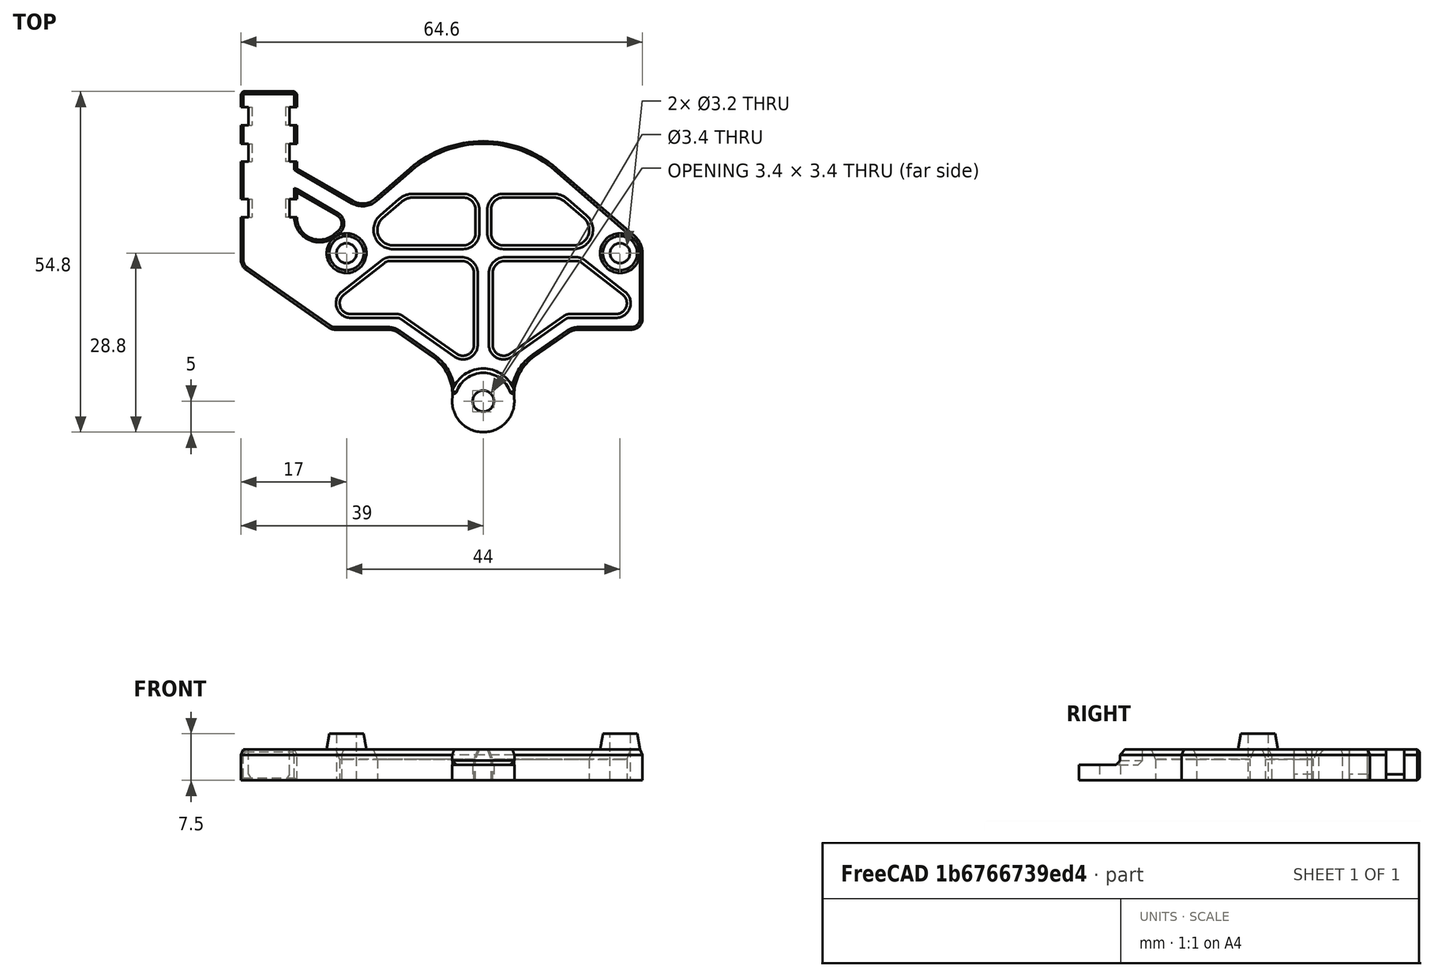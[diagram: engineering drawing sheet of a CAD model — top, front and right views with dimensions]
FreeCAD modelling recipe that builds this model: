
FCSTD DOCUMENT  (FreeCAD 0.21R33771 (Git))
Label: StrainRelief_v4
License: All rights reserved
LicenseURL: https://en.wikipedia.org/wiki/All_rights_reserved
objects: Sketcher::SketchObject×6, Part::Chamfer×5, PartDesign::Pad×3, PartDesign::Pocket×2, PartDesign::Body×2, Part::Fillet×2, Mesh::Feature×1, PartDesign::Mirrored×1, PartDesign::Chamfer×1, Part::Fuse×1
note: 29 computed .brp shape members not serialized (recipe doc carries the construction recipe); baked Part::Feature solids carry a one-line shape summary decoded from their .brp

FEATURE [Mesh::Feature] EBB36_Mount___Sherpa_Mini  label="EBB36 Mount - Sherpa-Mini"
  Placement = pos=(-216.5,184.28,0) rot=(0,0,1;4.71239rad)
FEATURE [Sketcher::SketchObject] Sketch
  FullyConstrained = true
  MapMode = 5
  Support = -> [XY_Plane]
  sketch-geometry (31):
    g0: ArcOfCircle CenterX=0 CenterY=-23.8 CenterZ=0 NormalX=0 NormalY=0 NormalZ=1 AngleXU=0 Radius=1.7 StartAngle=1.5708 EndAngle=4.71239
    g1: LineSegment StartX=-15.35 StartY=-12.3 StartZ=0 EndX=-23.85 EndY=-12.3 EndZ=0
    g2: ArcOfCircle CenterX=-23.85 CenterY=-10.55 CenterZ=0 NormalX=0 NormalY=0 NormalZ=1 AngleXU=0 Radius=1.75 StartAngle=3.14159 EndAngle=4.71239
    g3: LineSegment StartX=-25.6 StartY=-10.55 StartZ=0 EndX=-25.6 EndY=0 EndZ=0
    g4: ArcOfCircle CenterX=-22 CenterY=0 CenterZ=0 NormalX=0 NormalY=0 NormalZ=1 AngleXU=0 Radius=3.6 StartAngle=2.28438 EndAngle=3.14159
    g5: ArcOfCircle CenterX=0 CenterY=0 CenterZ=0 NormalX=0 NormalY=0 NormalZ=1 AngleXU=0 Radius=18 StartAngle=1.5708 EndAngle=2.28438
    g6: LineSegment StartX=0 StartY=18 StartZ=0 EndX=0 EndY=-22.1 EndZ=0
    g7: LineSegment StartX=-3e-16 StartY=-25.5 StartZ=0 EndX=0 EndY=-28.8 EndZ=0
    g8: ArcOfCircle CenterX=0 CenterY=-23.8 CenterZ=0 NormalX=0 NormalY=0 NormalZ=1 AngleXU=0 Radius=5 StartAngle=3.06281 EndAngle=4.71239
    g9: ArcOfCircle CenterX=-12.4612 CenterY=-22.8162 CenterZ=0 NormalX=0 NormalY=0 NormalZ=1 AngleXU=0 Radius=7.5 StartAngle=6.2044 EndAngle=7.24312
    g10: LineSegment StartX=-8.1594 StartY=-16.6726 StartZ=0 EndX=-13.6293 EndY=-12.8425 EndZ=0
    g11: LineSegment StartX=-12.9829 StartY=-10.0713 StartZ=0 EndX=-4.25376 EndY=-16.1835 EndZ=0
    g12: LineSegment StartX=-13.8433 StartY=-9.8 StartZ=0 EndX=-21.35 EndY=-9.8 EndZ=0
    g13: ArcOfCircle CenterX=-21.35 CenterY=-8.05 CenterZ=0 NormalX=0 NormalY=0 NormalZ=1 AngleXU=0 Radius=1.75 StartAngle=2.23402 EndAngle=4.71239
    g14: LineSegment StartX=-22.4274 StartY=-6.67098 StartZ=0 EndX=-15.8959 EndY=-1.56798 EndZ=0
    g15: LineSegment StartX=-14.9724 StartY=-1.25 StartZ=0 EndX=-3.5 EndY=-1.25 EndZ=0
    g16: ArcOfCircle CenterX=-3.5 CenterY=-3.25 CenterZ=0 NormalX=0 NormalY=0 NormalZ=1 AngleXU=0 Radius=2 StartAngle=1e-16 EndAngle=1.5708
    g17: LineSegment StartX=-1.5 StartY=-3.25 StartZ=0 EndX=-1.5 EndY=-14.75 EndZ=0
    g18: ArcOfCircle CenterX=-3.25 CenterY=-14.75 CenterZ=0 NormalX=0 NormalY=0 NormalZ=1 AngleXU=0 Radius=1.75 StartAngle=4.10152 EndAngle=6.28319
    g19: LineSegment StartX=-1.25 StartY=6.95 StartZ=0 EndX=-1.25 EndY=3.25 EndZ=0
    g20: ArcOfCircle CenterX=-3.25 CenterY=3.25 CenterZ=0 NormalX=0 NormalY=0 NormalZ=1 AngleXU=0 Radius=2 StartAngle=4.71239 EndAngle=6.28319
    g21: LineSegment StartX=-3.25 StartY=1.25 StartZ=0 EndX=-14.5429 EndY=1.25 EndZ=0
    g22: ArcOfCircle CenterX=-3.25 CenterY=6.95 CenterZ=0 NormalX=0 NormalY=0 NormalZ=1 AngleXU=0 Radius=2 StartAngle=2e-16 EndAngle=1.5708
    g23: LineSegment StartX=-3.25 StartY=8.95 StartZ=0 EndX=-11.25 EndY=8.95 EndZ=0
    g24: ArcOfCircle CenterX=-14.5429 CenterY=3.75 CenterZ=0 NormalX=0 NormalY=0 NormalZ=1 AngleXU=0 Radius=2.5 StartAngle=2.28638 EndAngle=4.71239
    g25: ArcOfCircle CenterX=-11.25 CenterY=5.95 CenterZ=0 NormalX=0 NormalY=0 NormalZ=1 AngleXU=0 Radius=3 StartAngle=1.5708 EndAngle=2.28638
    g26: LineSegment StartX=-16.1831 StartY=5.63677 StartZ=0 EndX=-13.2182 EndY=8.21413 EndZ=0
    g27: ArcOfCircle CenterX=-13.8433 CenterY=-11.3 CenterZ=0 NormalX=0 NormalY=0 NormalZ=1 AngleXU=0 Radius=1.5 StartAngle=0.959931 EndAngle=1.5708
    g28: ArcOfCircle CenterX=-15.35 CenterY=-15.3 CenterZ=0 NormalX=0 NormalY=0 NormalZ=1 AngleXU=0 Radius=3 StartAngle=0.959931 EndAngle=1.5708
    g29: ArcOfCircle CenterX=-14.9724 CenterY=-2.75 CenterZ=0 NormalX=0 NormalY=0 NormalZ=1 AngleXU=0 Radius=1.5 StartAngle=1.5708 EndAngle=2.23402
    g30: LineSegment StartX=-24.3564 StartY=2.72168 StartZ=0 EndX=-11.7818 EndY=13.6084 EndZ=0
  constraints (79):
    c: PointOnObject(g0,g-2)
    c: Diameter(g0) = 3.4
    c: Horizontal(g1)
    c: Tangent(g1,g2) = 1.5708
    c: PointOnObject(g3,g-1)
    c: Tangent(g3,g4) = 1.5708
    c: PointOnObject(g5,g-2)
    c: DistanceY(g5,g5) = 18
    c: DistanceY(g1,g5) = 12.3
    c: Tangent(g2,g3) = 1.5708
    c: Coincident(g6,g5)
    c: Vertical(g6)
    c: Perpendicular(g7,g8) = 1.5708
    c: Coincident(g8,g0)
    c: PointOnObject(g7,g-2)
    c: Coincident(g0,g7)
    c: Coincident(g0,g6)
    c: Coincident(g5,g-1)
    c: DistanceY(g0,g5) = 23.8
    c: Diameter(g8) = 10
    c: Tangent(g8,g9) = 1.5708
    c: Tangent(g9,g10) = -1.5708
    c: Angle(g6,g10) = 0.959931
    c: Diameter(g9) = 15
    c: Diameter(g2) = 3.5
    c: Parallel(g11,g10)
    c: Horizontal(g12)
    c: Tangent(g12,g13) = 1.5708
    c: Horizontal(g15)
    c: Tangent(g15,g16) = 1.5708
    c: Vertical(g17)
    c: Diameter(g16) = 4
    c: Tangent(g13,g14) = 1.5708
    c: Tangent(g16,g17) = 1.5708
    c: DistanceY(g15,g5) = 1.25
    c: DistanceX(g16,g5) = 1.5
    c: Tangent(g18,g17) = 1.5708
    c: Tangent(g18,g11) = -1.5708
    c: Diameter(g13) = 3.5
    c: DistanceX(g2,g13) = 4.25
    c: Diameter(g18) = 3.5
    c: Vertical(g19)
    c: Tangent(g19,g20) = 1.5708
    c: Tangent(g20,g21) = 1.5708
    c: Horizontal(g21)
    c: DistanceY(g5,g20) = 1.25
    c: DistanceX(g19,g5) = 1.25
    c: Diameter(g20) = 4
    c: Diameter(g22) = 4
    c: Horizontal(g23)
    c: Tangent(g23,g22) = -1.5708
    c: Tangent(g22,g19) = 1.5708
    c: Tangent(g24,g21) = 1.5708
    c: Tangent(g26,g24) = 1.5708
    c: Tangent(g26,g25) = 1.5708
    c: DistanceX(g23,g23) = 8
    c: Radius(g25) = 3
    c: Tangent(g25,g23) = -1.5708
    c: DistanceY(g19,g19) = 3.7
    c: Radius(g24) = 2.5
    c: Angle(g-1,g26) = 0.715585
    c: Tangent(g12,g27) = -1.5708
    c: Tangent(g11,g27) = 1.5708
    c: Tangent(g1,g28) = -1.5708
    c: Tangent(g10,g28) = -1.5708
    c: Tangent(g14,g29) = 1.5708
    c: Tangent(g15,g29) = 1.5708
    c: Radius(g29) = 1.5
    c: Radius(g27) = 1.5
    c: Radius(g28) = 3
    c: DistanceY(g1,g12) = 2.5
    c: DistanceY(g17,g17) = 11.5
    c: DistanceX(g1,g1) = 8.5
    c: Angle(g14,g6) = 0.907571
    c: DistanceX(g3,g5) = 25.6
    c: PointOnObject(g4,g-1)
    c: Diameter(g4) = 7.2
    c: Tangent(g30,g5) = 1.5708
    c: Tangent(g30,g4) = 1.5708
FEATURE [PartDesign::Pad] Pad
  Direction = (0,0,1)
  Length = 5
  Length2 = 10
  Profile = -> Sketch
  ReferenceAxis = -> Sketch [N_Axis]
  Type = 0
FEATURE [Sketcher::SketchObject] Sketch001
  AttachmentOffset = pos=(0,0,7.5) rot=(0,0,1;0rad)
  FullyConstrained = false
  MapMode = 5
  Placement = pos=(0,0,7.5) rot=(0,0,1;0rad)
  Support = -> [XY_Plane]
  sketch-geometry (1):
    g0: Circle CenterX=-22 CenterY=0 CenterZ=0 NormalX=0 NormalY=0 NormalZ=1 AngleXU=0 Radius=2.75
  constraints (2):
    c: Diameter(g0) = 5.5
    c: DistanceX(g0,g-1) = 22
FEATURE [PartDesign::Pad] Pad001
  BaseFeature = -> Pad
  Direction = (0,0,1)
  Length = 2.5
  Length2 = 10
  Profile = -> Sketch001
  ReferenceAxis = -> Sketch001 [N_Axis]
  Reversed = true
  TaperAngle = 10
  Type = 0
FEATURE [Sketcher::SketchObject] Sketch002
  FullyConstrained = true
  MapMode = 5
  Support = -> [XY_Plane]
  sketch-geometry (1):
    g0: Circle CenterX=-22 CenterY=0 CenterZ=0 NormalX=0 NormalY=0 NormalZ=1 AngleXU=0 Radius=1.6
  constraints (3):
    c: PointOnObject(g0,g-1)
    c: DistanceX(g0,g-1) = 22
    c: Diameter(g0) = 3.2
FEATURE [PartDesign::Pocket] Pocket
  BaseFeature = -> Pad001
  Direction = (0,0,-1)
  Length = 5
  Length2 = 5
  Profile = -> Sketch002
  ReferenceAxis = -> Sketch002 [N_Axis]
  Reversed = true
  Type = 1
FEATURE [PartDesign::Mirrored] Mirrored
  BaseFeature = -> Pocket
  MirrorPlane = -> Sketch [V_Axis]
  Originals = -> [Pad,Pad001,Pocket]
FEATURE [Sketcher::SketchObject] Sketch004
  FullyConstrained = true
  MapMode = 5
  Support = -> [XY_Plane001]
  sketch-geometry (31):
    g0: ArcOfCircle CenterX=0 CenterY=-23.8 CenterZ=0 NormalX=0 NormalY=0 NormalZ=1 AngleXU=0 Radius=1.7 StartAngle=1.5708 EndAngle=4.71239
    g1: LineSegment StartX=-15.35 StartY=-12.3 StartZ=0 EndX=-23.85 EndY=-12.3 EndZ=0
    g2: ArcOfCircle CenterX=-23.85 CenterY=-10.55 CenterZ=0 NormalX=0 NormalY=0 NormalZ=1 AngleXU=0 Radius=1.75 StartAngle=3.14159 EndAngle=4.71239
    g3: LineSegment StartX=-25.6 StartY=-10.55 StartZ=0 EndX=-25.6 EndY=0 EndZ=0
    g4: ArcOfCircle CenterX=-22 CenterY=0 CenterZ=0 NormalX=0 NormalY=0 NormalZ=1 AngleXU=0 Radius=3.6 StartAngle=2.28438 EndAngle=3.14159
    g5: ArcOfCircle CenterX=0 CenterY=0 CenterZ=0 NormalX=0 NormalY=0 NormalZ=1 AngleXU=0 Radius=18 StartAngle=1.5708 EndAngle=2.28438
    g6: LineSegment StartX=1e-16 StartY=18 StartZ=0 EndX=1e-16 EndY=-22.1 EndZ=0
    g7: LineSegment StartX=-2e-16 StartY=-25.5 StartZ=0 EndX=-9e-16 EndY=-28.8 EndZ=0
    g8: ArcOfCircle CenterX=0 CenterY=-23.8 CenterZ=0 NormalX=0 NormalY=0 NormalZ=1 AngleXU=0 Radius=5 StartAngle=3.06281 EndAngle=4.71239
    g9: ArcOfCircle CenterX=-12.4612 CenterY=-22.8162 CenterZ=0 NormalX=0 NormalY=0 NormalZ=1 AngleXU=0 Radius=7.5 StartAngle=6.2044 EndAngle=7.24312
    g10: LineSegment StartX=-8.1594 StartY=-16.6726 StartZ=0 EndX=-13.6293 EndY=-12.8425 EndZ=0
    g11: LineSegment StartX=-12.9829 StartY=-10.0713 StartZ=0 EndX=-4.25376 EndY=-16.1835 EndZ=0
    g12: LineSegment StartX=-13.8433 StartY=-9.8 StartZ=0 EndX=-21.35 EndY=-9.8 EndZ=0
    g13: ArcOfCircle CenterX=-21.35 CenterY=-8.05 CenterZ=0 NormalX=0 NormalY=0 NormalZ=1 AngleXU=0 Radius=1.75 StartAngle=2.23402 EndAngle=4.71239
    g14: LineSegment StartX=-22.4274 StartY=-6.67098 StartZ=0 EndX=-15.8959 EndY=-1.56798 EndZ=0
    g15: LineSegment StartX=-14.9724 StartY=-1.25 StartZ=0 EndX=-3.5 EndY=-1.25 EndZ=0
    g16: ArcOfCircle CenterX=-3.5 CenterY=-3.25 CenterZ=0 NormalX=0 NormalY=0 NormalZ=1 AngleXU=0 Radius=2 StartAngle=0 EndAngle=1.5708
    g17: LineSegment StartX=-1.5 StartY=-3.25 StartZ=0 EndX=-1.5 EndY=-14.75 EndZ=0
    g18: ArcOfCircle CenterX=-3.25 CenterY=-14.75 CenterZ=0 NormalX=0 NormalY=0 NormalZ=1 AngleXU=0 Radius=1.75 StartAngle=4.10152 EndAngle=6.28319
    g19: LineSegment StartX=-1.25 StartY=6.95 StartZ=0 EndX=-1.25 EndY=3.25 EndZ=0
    g20: ArcOfCircle CenterX=-3.25 CenterY=3.25 CenterZ=0 NormalX=0 NormalY=0 NormalZ=1 AngleXU=0 Radius=2 StartAngle=4.71239 EndAngle=6.28319
    g21: LineSegment StartX=-3.25 StartY=1.25 StartZ=0 EndX=-14.5429 EndY=1.25 EndZ=0
    g22: ArcOfCircle CenterX=-3.25 CenterY=6.95 CenterZ=0 NormalX=0 NormalY=0 NormalZ=1 AngleXU=0 Radius=2 StartAngle=0 EndAngle=1.5708
    g23: LineSegment StartX=-3.25 StartY=8.95 StartZ=0 EndX=-11.25 EndY=8.95 EndZ=0
    g24: ArcOfCircle CenterX=-14.5429 CenterY=3.75 CenterZ=0 NormalX=0 NormalY=0 NormalZ=1 AngleXU=0 Radius=2.5 StartAngle=2.28638 EndAngle=4.71239
    g25: ArcOfCircle CenterX=-11.25 CenterY=5.95 CenterZ=0 NormalX=0 NormalY=0 NormalZ=1 AngleXU=0 Radius=3 StartAngle=1.5708 EndAngle=2.28638
    g26: LineSegment StartX=-16.1831 StartY=5.63677 StartZ=0 EndX=-13.2182 EndY=8.21413 EndZ=0
    g27: ArcOfCircle CenterX=-13.8433 CenterY=-11.3 CenterZ=0 NormalX=0 NormalY=0 NormalZ=1 AngleXU=0 Radius=1.5 StartAngle=0.959931 EndAngle=1.5708
    g28: ArcOfCircle CenterX=-15.35 CenterY=-15.3 CenterZ=0 NormalX=0 NormalY=0 NormalZ=1 AngleXU=0 Radius=3 StartAngle=0.959931 EndAngle=1.5708
    g29: ArcOfCircle CenterX=-14.9724 CenterY=-2.75 CenterZ=0 NormalX=0 NormalY=0 NormalZ=1 AngleXU=0 Radius=1.5 StartAngle=1.5708 EndAngle=2.23402
    g30: LineSegment StartX=-24.3564 StartY=2.72168 StartZ=0 EndX=-11.7818 EndY=13.6084 EndZ=0
  constraints (79):
    c: PointOnObject(g0,g-2)
    c: Diameter(g0) = 3.4
    c: Horizontal(g1)
    c: Tangent(g1,g2) = 1.5708
    c: PointOnObject(g3,g-1)
    c: Tangent(g3,g4) = 1.5708
    c: PointOnObject(g5,g-2)
    c: DistanceY(g5,g5) = 18
    c: DistanceY(g1,g5) = 12.3
    c: Tangent(g2,g3) = 1.5708
    c: Coincident(g6,g5)
    c: Vertical(g6)
    c: Perpendicular(g7,g8) = 1.5708
    c: Coincident(g8,g0)
    c: PointOnObject(g7,g-2)
    c: Coincident(g0,g7)
    c: Coincident(g0,g6)
    c: Coincident(g5,g-1)
    c: DistanceY(g0,g5) = 23.8
    c: Diameter(g8) = 10
    c: Tangent(g8,g9) = 1.5708
    c: Tangent(g9,g10) = -1.5708
    c: Angle(g6,g10) = 0.959931
    c: Diameter(g9) = 15
    c: Diameter(g2) = 3.5
    c: Parallel(g11,g10)
    c: Horizontal(g12)
    c: Tangent(g12,g13) = 1.5708
    c: Horizontal(g15)
    c: Tangent(g15,g16) = 1.5708
    c: Vertical(g17)
    c: Diameter(g16) = 4
    c: Tangent(g13,g14) = 1.5708
    c: Tangent(g16,g17) = 1.5708
    c: DistanceY(g15,g5) = 1.25
    c: DistanceX(g16,g5) = 1.5
    c: Tangent(g18,g17) = 1.5708
    c: Tangent(g18,g11) = -1.5708
    c: Diameter(g13) = 3.5
    c: DistanceX(g2,g13) = 4.25
    c: Diameter(g18) = 3.5
    c: Vertical(g19)
    c: Tangent(g19,g20) = 1.5708
    c: Tangent(g20,g21) = 1.5708
    c: Horizontal(g21)
    c: DistanceY(g5,g20) = 1.25
    c: DistanceX(g19,g5) = 1.25
    c: Diameter(g20) = 4
    c: Diameter(g22) = 4
    c: Horizontal(g23)
    c: Tangent(g23,g22) = -1.5708
    c: Tangent(g22,g19) = 1.5708
    c: Tangent(g24,g21) = 1.5708
    c: Tangent(g26,g24) = 1.5708
    c: Tangent(g26,g25) = 1.5708
    c: DistanceX(g23,g23) = 8
    c: Radius(g25) = 3
    c: Tangent(g25,g23) = -1.5708
    c: DistanceY(g19,g19) = 3.7
    c: Radius(g24) = 2.5
    c: Angle(g-1,g26) = 0.715585
    c: Tangent(g12,g27) = -1.5708
    c: Tangent(g11,g27) = 1.5708
    c: Tangent(g1,g28) = -1.5708
    c: Tangent(g10,g28) = -1.5708
    c: Tangent(g14,g29) = 1.5708
    c: Tangent(g15,g29) = 1.5708
    c: Radius(g29) = 1.5
    c: Radius(g27) = 1.5
    c: Radius(g28) = 3
    c: DistanceY(g1,g12) = 2.5
    c: DistanceY(g17,g17) = 11.5
    c: DistanceX(g1,g1) = 8.5
    c: Angle(g14,g6) = 0.907571
    c: DistanceX(g3,g5) = 25.6
    c: PointOnObject(g4,g-1)
    c: Diameter(g4) = 7.2
    c: Tangent(g30,g5) = 1.5708
    c: Tangent(g30,g4) = 1.5708
FEATURE [Sketcher::SketchObject] Sketch005
  ExternalGeometry = -> [Sketch004]
  FullyConstrained = true
  MapMode = 5
  Support = -> [XY_Plane001]
  sketch-geometry (38):
    g0: LineSegment StartX=-39 StartY=26 StartZ=0 EndX=-30 EndY=26 EndZ=0
    g1: LineSegment StartX=-30 StartY=26 StartZ=0 EndX=-30 EndY=-7 EndZ=0
    g2: LineSegment StartX=-30 StartY=-7 StartZ=0 EndX=-39 EndY=-7 EndZ=0
    g3: LineSegment StartX=-39 StartY=-7 StartZ=0 EndX=-39 EndY=26 EndZ=0
    g4: LineSegment StartX=-38.1472 StartY=-2.67538 StartZ=0 EndX=-24.8538 EndY=-11.9835 EndZ=0
    g5: LineSegment StartX=-39 StartY=26 StartZ=0 EndX=-30 EndY=26 EndZ=0
    g6: LineSegment StartX=-30 StartY=26 StartZ=0 EndX=-30 EndY=23.5 EndZ=0
    g7: LineSegment StartX=-30 StartY=23.5 StartZ=0 EndX=-31.2 EndY=23.5 EndZ=0
    g8: LineSegment StartX=-31.2 StartY=23.5 StartZ=0 EndX=-31.2 EndY=20.6 EndZ=0
    g9: LineSegment StartX=-31.2 StartY=20.6 StartZ=0 EndX=-30 EndY=20.6 EndZ=0
    g10: LineSegment StartX=-30 StartY=20.6 StartZ=0 EndX=-30 EndY=17.6 EndZ=0
    g11: LineSegment StartX=-30 StartY=17.6 StartZ=0 EndX=-31.2 EndY=17.6 EndZ=0
    g12: LineSegment StartX=-31.2 StartY=17.6 StartZ=0 EndX=-31.2 EndY=14.7 EndZ=0
    g13: LineSegment StartX=-31.2 StartY=14.7 StartZ=0 EndX=-30 EndY=14.7 EndZ=0
    g14: LineSegment StartX=-30 StartY=14.7 StartZ=0 EndX=-30 EndY=13.6093 EndZ=0
    g15: LineSegment StartX=-30 StartY=8.7 StartZ=0 EndX=-31.2 EndY=8.7 EndZ=0
    g16: LineSegment StartX=-31.2 StartY=8.7 StartZ=0 EndX=-31.2 EndY=5.8 EndZ=0
    g17: LineSegment StartX=-31.2 StartY=5.8 StartZ=0 EndX=-30 EndY=5.8 EndZ=0
    g18: ArcOfCircle CenterX=-26.3608 CenterY=5.8 CenterZ=0 NormalX=0 NormalY=0 NormalZ=1 AngleXU=0 Radius=3.63924 StartAngle=3.14159 EndAngle=5.42597
    g19: LineSegment StartX=-39 StartY=26 StartZ=0 EndX=-39 EndY=23.5 EndZ=0
    g20: LineSegment StartX=-39 StartY=23.5 StartZ=0 EndX=-37.8 EndY=23.5 EndZ=0
    g21: LineSegment StartX=-37.8 StartY=23.5 StartZ=0 EndX=-37.8 EndY=20.6 EndZ=0
    g22: LineSegment StartX=-37.8 StartY=20.6 StartZ=0 EndX=-39 EndY=20.6 EndZ=0
    g23: LineSegment StartX=-39 StartY=20.6 StartZ=0 EndX=-39 EndY=17.6 EndZ=0
    g24: LineSegment StartX=-39 StartY=17.6 StartZ=0 EndX=-37.8 EndY=17.6 EndZ=0
    g25: LineSegment StartX=-37.8 StartY=17.6 StartZ=0 EndX=-37.8 EndY=14.7 EndZ=0
    g26: LineSegment StartX=-37.8 StartY=14.7 StartZ=0 EndX=-39 EndY=14.7 EndZ=0
    g27: LineSegment StartX=-39 StartY=14.7 StartZ=0 EndX=-39 EndY=8.7 EndZ=0
    g28: LineSegment StartX=-39 StartY=8.7 StartZ=0 EndX=-37.8 EndY=8.7 EndZ=0
    g29: LineSegment StartX=-37.8 StartY=8.7 StartZ=0 EndX=-37.8 EndY=5.8 EndZ=0
    g30: LineSegment StartX=-37.8 StartY=5.8 StartZ=0 EndX=-39 EndY=5.8 EndZ=0
    g31: LineSegment StartX=-39 StartY=5.8 StartZ=0 EndX=-39 EndY=-1.03708 EndZ=0
    g32: LineSegment StartX=-23.9787 StartY=3.04865 StartZ=0 EndX=-24.8538 EndY=-11.9835 EndZ=0
    g33: LineSegment StartX=-30 StartY=9.79069 StartZ=0 EndX=-21.2575 EndY=4.74322 EndZ=0
    g34: LineSegment StartX=-18.6114 StartY=7.03413 StartZ=0 EndX=-30 EndY=13.6093 EndZ=0
    g35: LineSegment StartX=-30 StartY=9.79069 StartZ=0 EndX=-30 EndY=8.7 EndZ=0
    g36: LineSegment StartX=-18.6114 StartY=7.03413 StartZ=0 EndX=-21.2575 EndY=4.74322 EndZ=0
    g37: ArcOfCircle CenterX=-37 CenterY=-1.03708 CenterZ=0 NormalX=0 NormalY=0 NormalZ=1 AngleXU=0 Radius=2 StartAngle=3.14159 EndAngle=4.10152
  constraints (110):
    c: Coincident(g0,g1)
    c: Coincident(g1,g2)
    c: Coincident(g2,g3)
    c: Coincident(g3,g0)
    c: DistanceY(g1,g1) = 33
    c: DistanceX(g0,g0) = 9
    c: Parallel(g4,g-3)
    c: DistanceX(g1,g-1) = 30
    c: Coincident(g0,g5)
    c: Coincident(g5,g0)
    c: Coincident(g5,g6)
    c: PointOnObject(g6,g1)
    c: Coincident(g6,g7)
    c: Coincident(g7,g8)
    c: Vertical(g8)
    c: Coincident(g8,g9)
    c: PointOnObject(g9,g1)
    c: Coincident(g9,g10)
    c: PointOnObject(g10,g1)
    c: Coincident(g10,g11)
    c: Horizontal(g11)
    c: Coincident(g11,g12)
    c: Vertical(g12)
    c: Coincident(g12,g13)
    c: PointOnObject(g13,g1)
    c: Coincident(g13,g14)
    c: PointOnObject(g35,g1)
    c: Coincident(g35,g15)
    c: Coincident(g15,g16)
    c: Vertical(g16)
    c: Coincident(g16,g17)
    c: PointOnObject(g17,g1)
    c: Horizontal(g17)
    c: Coincident(g18,g17)
    c: Perpendicular(g18,g17)
    c: Horizontal(g7)
    c: Horizontal(g9)
    c: Horizontal(g13)
    c: Horizontal(g15)
    c: Equal(g16,g12)
    c: Equal(g12,g8)
    c: Equal(g7,g11)
    c: Equal(g11,g15)
    c: DistanceX(g7,g7) = 1.2
    c: DistanceY(g16,g16) = 2.9
    c: DistanceY(g6,g6) = 2.5
    c: DistanceY(g10,g10) = 3
    c: Horizontal(g5,g5)
    c: Coincident(g5,g19)
    c: PointOnObject(g19,g3)
    c: Coincident(g19,g20)
    c: Horizontal(g20)
    c: Coincident(g20,g21)
    c: Coincident(g21,g22)
    c: PointOnObject(g22,g3)
    c: Coincident(g22,g23)
    c: PointOnObject(g23,g3)
    c: Coincident(g23,g24)
    c: Coincident(g24,g25)
    c: Coincident(g25,g26)
    c: PointOnObject(g26,g3)
    c: Coincident(g26,g27)
    c: PointOnObject(g27,g3)
    c: Vertical(g27)
    c: Coincident(g27,g28)
    c: Coincident(g28,g29)
    c: Coincident(g29,g30)
    c: PointOnObject(g30,g3)
    c: Coincident(g30,g31)
    c: Horizontal(g20,g7)
    c: Equal(g21,g8)
    c: Equal(g25,g12)
    c: Vertical(g25)
    c: Vertical(g29)
    c: Horizontal(g28)
    c: Horizontal(g30)
    c: Horizontal(g26)
    c: Horizontal(g24)
    c: Horizontal(g22)
    c: Horizontal(g24,g11)
    c: Horizontal(g28,g15)
    c: Equal(g24,g22)
    c: Equal(g22,g28)
    c: Equal(g20,g7)
    c: Vertical(g21)
    c: Equal(g29,g16)
    c: DistanceY(g-1,g5) = 26
    c: Coincident(g32,g18)
    c: Horizontal(g2)
    c: Coincident(g4,g32)
    c: Tangent(g4,g-4) = -1.5708
    c: Tangent(g18,g-6) = -1.5708
    c: Coincident(g33,g36) = -1.5708
    c: Coincident(g36,g34) = -1.5708
    c: Distance(g36,g36) = 3.5
    c: Angle(g-2,g34) = 1.0472
    c: DistanceY(g27,g27) = 6
    c: Equal(g14,g35)
    c: Coincident(g34,g14)
    c: Coincident(g33,g35)
    c: Vertical(g14)
    c: Parallel(g34,g33)
    c: Vertical(g35)
    c: Parallel(g36,g-6)
    c: Distance(g34,g-6) = 0.5
    c: Equal(g2,g5)
    c: Tangent(g31,g37) = -1.5708
    c: Tangent(g4,g37) = -1.5708
    c: Diameter(g37) = 4
    c: PointOnObject(g31,g3)
FEATURE [PartDesign::Pad] Pad002
  Direction = (0,0,1)
  Length = 5
  Length2 = 10
  Profile = -> Sketch005
  ReferenceAxis = -> Sketch005 [N_Axis]
  Type = 0
FEATURE [PartDesign::Body] Body001  label="StrainArm"
  Group = -> [Sketch005,Sketch004,Pad002]
  Origin = -> Origin001
  Tip = -> Pad002
FEATURE [Sketcher::SketchObject] Sketch007
  AttachmentOffset = pos=(0,0,5) rot=(0,0,1;0rad)
  ExternalGeometry = -> [Sketch]
  FullyConstrained = true
  MapMode = 5
  Placement = pos=(0,0,5) rot=(0,0,1;0rad)
  Support = -> [XY_Plane]
  expr: .AttachmentOffset.Base.z = Pad.Length
  sketch-geometry (1):
    g0: Circle CenterX=0 CenterY=-23.8 CenterZ=0 NormalX=0 NormalY=0 NormalZ=1 AngleXU=0 Radius=5.25
  constraints (2):
    c: Coincident(g0,g-3)
    c: Diameter(g0) = 10.5
FEATURE [PartDesign::Pocket] Pocket001
  BaseFeature = -> Mirrored
  Direction = (0,0,-1)
  Length = 2.5
  Length2 = 5
  Profile = -> Sketch007
  ReferenceAxis = -> Sketch007 [N_Axis]
  Type = 0
FEATURE [PartDesign::Chamfer] Chamfer
  Angle = 45
  Base = -> Pocket001 [Edge161]
  BaseFeature = -> Pocket001
  ChamferType = 0
  FlipDirection = false
  Size = 0.7
  Size2 = 1
  SupportTransform = false
  UseAllEdges = false
FEATURE [PartDesign::Body] Body  label="MainBody"
  Group = -> [Sketch,Pad,Sketch001,Pad001,Sketch002,Pocket,Mirrored,Sketch007,Pocket001,Chamfer]
  Origin = -> Origin
  Tip = -> Chamfer
FEATURE [Part::Fuse] Fusion
  Base = -> Body
  Refine = true
  Tool = -> Body001
FEATURE [Part::Chamfer] Chamfer001
  Base = -> Fusion
  Edges = 4 edges: [Edge147 r1=0.6 r2=1.6,Edge159 r1=0.6 r2=1.6,Edge165 r1=0.6 r2=1.6,Edge177 r1=0.6 r2=1.6]
FEATURE [Part::Fillet] Fillet
  Base = -> Chamfer001
  Edges = 1 edges r=3: [Edge138]
FEATURE [Part::Fillet] Fillet001
  Base = -> Fillet
  Edges = 1 edges r=1.5: [Edge207]
FEATURE [Part::Chamfer] Chamfer002
  Base = -> Fillet001
  Edges = 3 edges: [Edge7 r1=0.4 r2=0.9,Edge11 r1=0.4 r2=0.9,Edge38 r1=0.4 r2=0.9]
FEATURE [Part::Chamfer] Chamfer003
  Base = -> Chamfer002
  Edges = 7 edges: [Edge4 r1=0.4 r2=0.9,Edge75 r1=0.4 r2=0.9,Edge79 r1=0.4 r2=0.9,Edge83 r1=0.4 r2=0.9,Edge85 r1=0.4 r2=0.9,Edge89 r1=0.4 r2=0.9,Edge93 r1=0.4 r2=0.9]
FEATURE [Part::Chamfer] Chamfer004
  Base = -> Chamfer003
  Edges = 6 edges: [Edge105 r1=1 r2=0.6,Edge200 r1=1 r2=0.6,Edge215 r1=1 r2=0.6,Edge243 r1=1 r2=0.6,Edge261 r1=1 r2=0.6,Edge279 r1=1 r2=0.6]
FEATURE [Part::Chamfer] Chamfer005
  Base = -> Chamfer004
  Edges = 6 edges r=0.4: [Edge69,Edge201,Edge318,Edge320,Edge321,Edge322]
